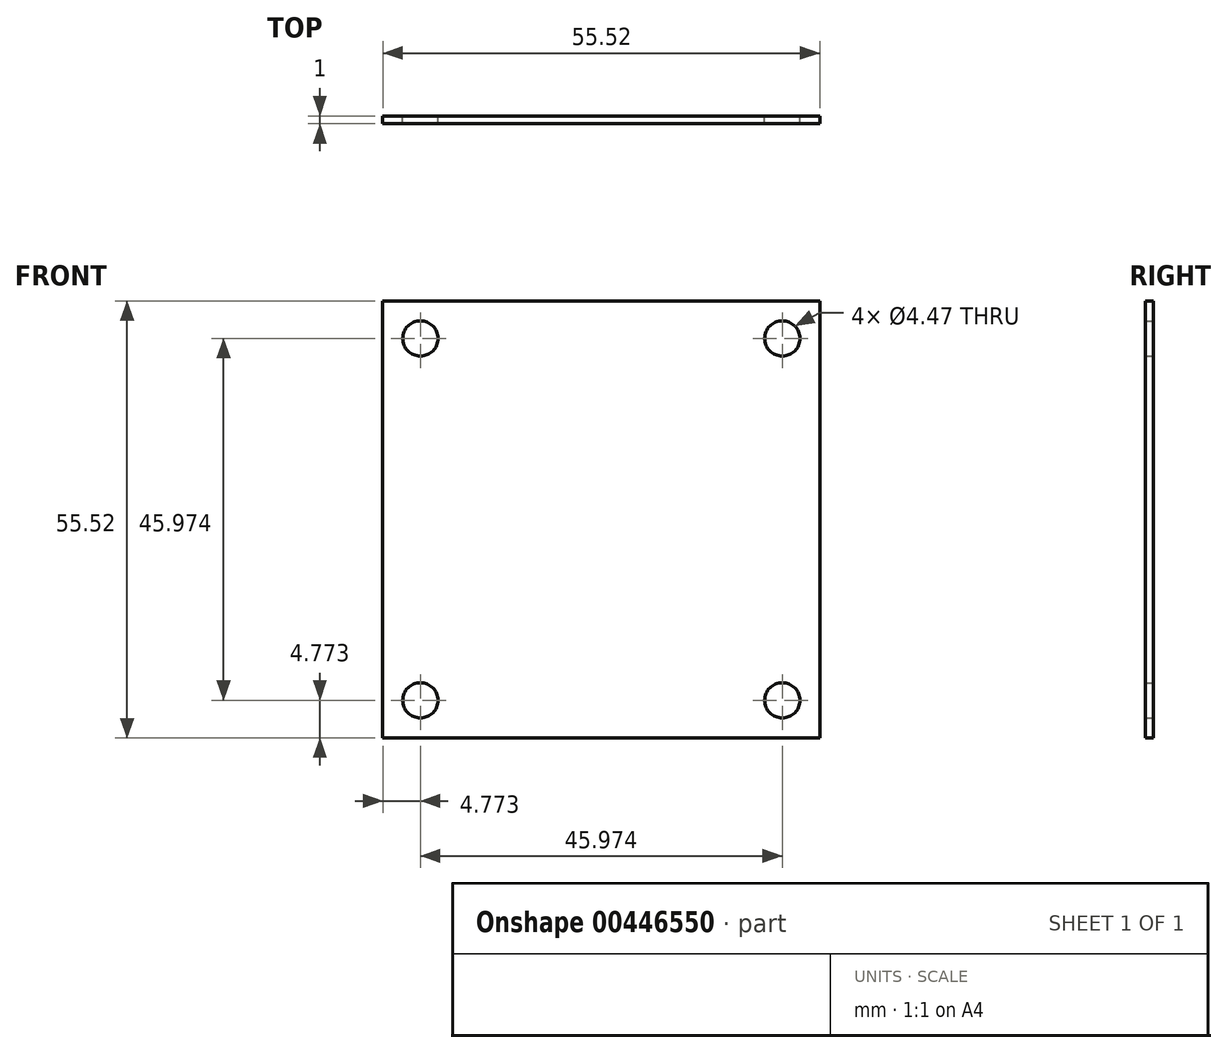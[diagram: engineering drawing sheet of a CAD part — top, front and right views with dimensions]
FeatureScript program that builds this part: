
annotation { "Feature Type Name" : "Feature", "Feature Type Description" : "" }
export const myFeature = defineFeature(function(context is Context, id is Id, definition is map)
    precondition{}
    {
        {
            var Q0;
            Q0=qCreatedBy(makeId("Front.planeOp"),FACE);
            var sketch = newSketch(context, id + "F0", { "sketchPlane" : qUnion([Q0])});
            skCircle(sketch, "E0", {"center": v(0, 0) * mm, "radius": 22.99 * mm, "construction": true});
            skLineSegment(sketch, "E1.bottom", {"start": v(-22.99, 22.99) * mm, "end": v(22.99, 22.99) * mm, "construction": true});
            skLineSegment(sketch, "E1.top", {"start": v(-22.99, -22.99) * mm, "end": v(22.99, -22.99) * mm, "construction": true});
            skLineSegment(sketch, "E1.left", {"start": v(-22.99, 22.99) * mm, "end": v(-22.99, -22.99) * mm, "construction": true});
            skLineSegment(sketch, "E1.right", {"start": v(22.99, 22.99) * mm, "end": v(22.99, -22.99) * mm, "construction": true});
            skCircle(sketch, "E2", {"center": v(22.99, -22.99) * mm, "radius": 2.24 * mm});
            skCircle(sketch, "E3", {"center": v(22.99, 22.99) * mm, "radius": 2.24 * mm});
            skCircle(sketch, "E4", {"center": v(-22.99, 22.99) * mm, "radius": 2.24 * mm});
            skCircle(sketch, "E5", {"center": v(-22.99, -22.99) * mm, "radius": 2.24 * mm});
            skLineSegment(sketch, "E6.bottom", {"start": v(27.76, -27.76) * mm, "end": v(-27.76, -27.76) * mm});
            skLineSegment(sketch, "E6.top", {"start": v(27.76, 27.76) * mm, "end": v(-27.76, 27.76) * mm});
            skLineSegment(sketch, "E6.left", {"start": v(27.76, -27.76) * mm, "end": v(27.76, 27.76) * mm});
            skLineSegment(sketch, "E6.right", {"start": v(-27.76, -27.76) * mm, "end": v(-27.76, 27.76) * mm});
            skSolve(sketch);
        }
        {
            var Q0;
            Q0 = qSketchRegion(id + "F0", true);
            extrude(context, id + "F1", {"entities" : qUnion([Q0]), "depth" : 1 * mm});
        }
    });
